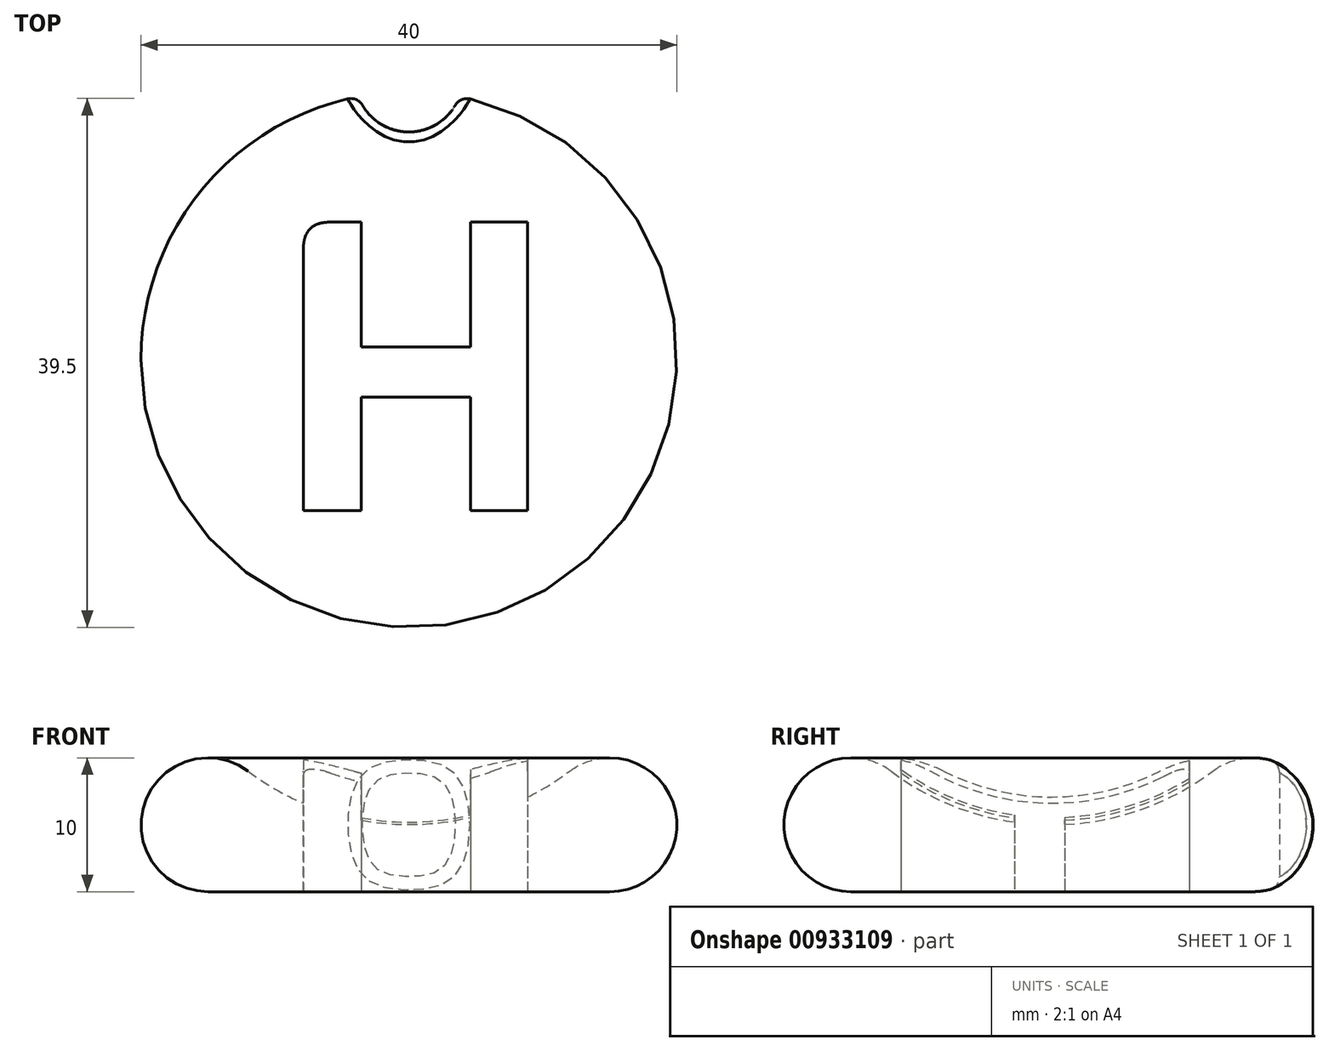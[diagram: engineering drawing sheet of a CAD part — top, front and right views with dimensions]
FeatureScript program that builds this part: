
annotation { "Feature Type Name" : "Feature", "Feature Type Description" : "" }
export const myFeature = defineFeature(function(context is Context, id is Id, definition is map)
    precondition{}
    {
        {
            var Q0;
            Q0=qCreatedBy(makeId("Front.planeOp"),FACE);
            var sketch = newSketch(context, id + "F0", { "sketchPlane" : qUnion([Q0])});
            skArc(sketch, "E0", {"start": v(-12, 9) * mm, "mid": v(-19.74, 6.58) * mm, "end": v(-15, 0) * mm});
            skArc(sketch, "E1", {"start": v(-12, 9) * mm, "mid": v(-6.32, 6.03) * mm, "end": v(0, 5) * mm});
            skLineSegment(sketch, "E2", {"start": v(-12.8, 0) * mm, "end": v(0, 0) * mm});
            skLineSegment(sketch, "E3", {"start": v(0, 0) * mm, "end": v(0, 5) * mm});
            skLineSegment(sketch, "E4", {"start": v(-15, 0) * mm, "end": v(-12.8, 0) * mm});
            skSolve(sketch);
        }
        {
            var Q0;
            Q0=makeQuery(id+"F0.imprint","IMPRINT",FACE,{"disambiguationData":[TD([[makeQuery(id+"F0.imprint","IMPRINT",EDGE,{"derivedFrom":sQuery(id+"F0.wireOp",EDGE,"E0")}),1.0]])]});
            var Q1;
            Q1=sQuery(id+"F0.wireOp",EDGE,"E3");
            revolve(context, id + "F1", {"surfaceOperationType" : NewSurfaceOperationType.NEW, "entities" : qUnion([Q0]), "axis" : qUnion([Q1]), "revolveType" : RevolveType.FULL});
        }
        {
            var Q0;
            Q0=makeQuery(id+"F1.opRevolve","SWEPT_FACE",FACE,{"disambiguationData":[OSD([sQuery(id+"F0.wireOp",EDGE,"E2"),sQuery(id+"F0.wireOp",EDGE,"E4")])]});
            var sketch = newSketch(context, id + "F2", { "sketchPlane" : qUnion([Q0])});
            skText(sketch, "E5", { "text": "H", "fontName": "NotoSansCJKjp-Bold.otf"});
            const initialGuessF2  = {"E5": [-0.01052, -0.01027, 1, 0, 0.02096]};
            skSetInitialGuess(sketch, initialGuessF2);
            skSolve(sketch);
        }
        {
            var Q0;
            Q0=makeQuery(id+"F2.imprint","IMPRINT",FACE,{"disambiguationData":[TD([[makeQuery(id+"F2.imprint","IMPRINT",EDGE,{"derivedFrom":sQuery(id+"F2.wireOp",EDGE,"E5.sketch_text.stroke-0")}),1.0]])]});
            extrude(context, id + "F3", {"entities" : qUnion([Q0]), "operationType" : NewBodyOperationType.REMOVE, "oppositeDirection" : true, "depth" : 25 * mm, "offsetDistance" : 25 * mm});
        }
        {
            var Q0;
            Q0=qCreatedBy(makeId("Top.planeOp"),FACE);
            var sketch = newSketch(context, id + "F4", { "sketchPlane" : qUnion([Q0])});
            skCircle(sketch, "E6", {"center": v(0, 21) * mm, "radius": 4 * mm});
            skSolve(sketch);
        }
        {
            var Q0;
            Q0=makeQuery(id+"F4.imprint","IMPRINT",FACE,{"disambiguationData":[TD([[makeQuery(id+"F4.imprint","IMPRINT",EDGE,{"derivedFrom":sQuery(id+"F4.wireOp",EDGE,"E6")}),1.0]])]});
            extrude(context, id + "F5", {"entities" : qUnion([Q0]), "operationType" : NewBodyOperationType.REMOVE, "endBound" : BoundingType.THROUGH_ALL, "depth" : 25 * mm, "offsetDistance" : 25 * mm});
        }
        {
            var Q0;
            Q0=makeQuery(id+"F5.boolean.opBoolean","INTERSECT",EDGE,{"derivedFrom":[makeQuery(id+"F1.opRevolve","SWEPT_FACE",FACE,{"disambiguationData":[OSD([sQuery(id+"F0.wireOp",EDGE,"E0")])]}),makeQuery(id+"F5.opExtrude","SWEPT_FACE",FACE,{"disambiguationData":[OSD([sQuery(id+"F4.wireOp",EDGE,"E6")])]})]});
            fillet(context, id + "F6", {"entities" : qUnion([Q0]), "radius" : 1 * mm, "tangentPropagation" : true, "allowEdgeOverflow" : false});
        }
        {
            var Q0;
            Q0=makeQuery(id+"F3.boolean.opBoolean","COPY",EDGE,{"derivedFrom":makeQuery(id+"F3.opExtrude","SWEPT_EDGE",EDGE,{"disambiguationData":[OSD([sQuery(id+"F2.wireOp",EDGE,"E5.sketch_text.stroke-0"),sQuery(id+"F2.wireOp",EDGE,"E5.sketch_text.stroke-11")])]})});
            fillet(context, id + "F7", {"entities" : qUnion([Q0]), "radius" : 2 * mm, "tangentPropagation" : true, "rho" : 0.5, "crossSection" : FilletCrossSection.CONIC, "allowEdgeOverflow" : false});
        }
    });
